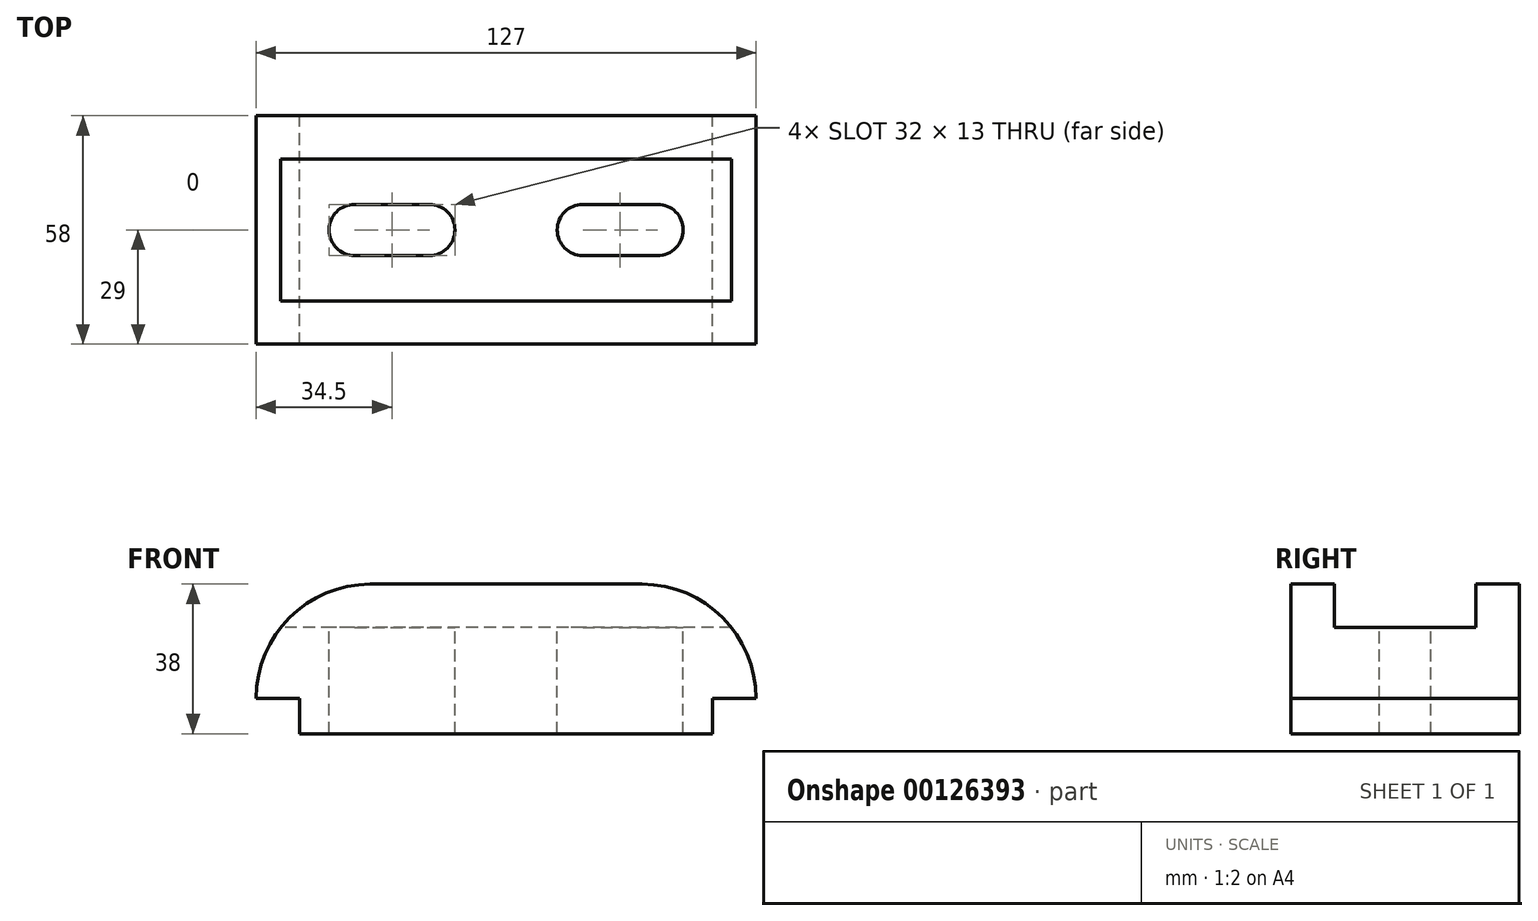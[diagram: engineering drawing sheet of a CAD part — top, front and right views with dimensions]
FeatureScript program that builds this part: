
annotation { "Feature Type Name" : "Feature", "Feature Type Description" : "" }
export const myFeature = defineFeature(function(context is Context, id is Id, definition is map)
    precondition{}
    {
        {
            var Q0;
            Q0=qCreatedBy(makeId("Front.planeOp"),FACE);
            var sketch = newSketch(context, id + "F0", { "sketchPlane" : qUnion([Q0])});
            skLineSegment(sketch, "E0.bottom", {"start": v(0, 0) * mm, "end": v(127, 0) * mm});
            skLineSegment(sketch, "E0.top", {"start": v(29, 38) * mm, "end": v(98, 38) * mm});
            skLineSegment(sketch, "E0.left", {"start": v(0, 0) * mm, "end": v(0, 9) * mm});
            skLineSegment(sketch, "E0.right", {"start": v(127, 0) * mm, "end": v(127, 9) * mm});
            skLineSegment(sketch, "E1", {"start": v(0, 9) * mm, "end": v(11, 9) * mm});
            skLineSegment(sketch, "E2", {"start": v(11, 9) * mm, "end": v(11, 0) * mm});
            skLineSegment(sketch, "E3.bottom", {"start": v(127, 0) * mm, "end": v(116, 0) * mm});
            skLineSegment(sketch, "E3.top", {"start": v(127, 9) * mm, "end": v(116, 9) * mm});
            skLineSegment(sketch, "E3.right", {"start": v(116, 0) * mm, "end": v(116, 9) * mm});
            skArc(sketch, "E4", {"start": v(0, 9) * mm, "mid": v(8.5, 29.5) * mm, "end": v(29, 38) * mm});
            skPoint(sketch, "E4.centerSnap0", {"position": v(5.5, 9) * mm});
            skArc(sketch, "E5", {"start": v(127, 9) * mm, "mid": v(118.5, 29.5) * mm, "end": v(98, 38) * mm});
            skSolve(sketch);
        }
        {
            var Q0;
            Q0=makeQuery(id+"F0.imprint","IMPRINT",FACE,{"disambiguationData":[TD([[makeQuery(id+"F0.imprint","IMPRINT",EDGE,{"derivedFrom":sQuery(id+"F0.wireOp",EDGE,"E0.top")}),-1.0]])]});
            extrude(context, id + "F1", {"entities" : qUnion([Q0]), "endBound" : BoundingType.SYMMETRIC, "depth" : 58 * mm});
        }
        {
            var Q0;
            Q0=makeQuery(id+"F1.opExtrude","SWEPT_FACE",FACE,{"disambiguationData":[OSD([sQuery(id+"F0.wireOp",EDGE,"E0.top")])]});
            var sketch = newSketch(context, id + "F2", { "sketchPlane" : qUnion([Q0])});
            skArc(sketch, "E6", {"start": v(25, 6.5) * mm, "mid": v(18.5, 0) * mm, "end": v(25, -6.5) * mm});
            skPoint(sketch, "E6.centerSnap0", {"position": v(29, 0) * mm});
            skArc(sketch, "E7", {"start": v(44, -6.5) * mm, "mid": v(50.5, 0) * mm, "end": v(44, 6.5) * mm});
            skArc(sketch, "E8", {"start": v(83, 6.5) * mm, "mid": v(76.5, 0) * mm, "end": v(83, -6.5) * mm});
            skArc(sketch, "E9", {"start": v(102, -6.5) * mm, "mid": v(108.5, 0) * mm, "end": v(102, 6.5) * mm});
            skLineSegment(sketch, "E10", {"start": v(25, 6.5) * mm, "end": v(44, 6.5) * mm});
            skLineSegment(sketch, "E11", {"start": v(25, -6.5) * mm, "end": v(44, -6.5) * mm});
            skLineSegment(sketch, "E12", {"start": v(83, 6.5) * mm, "end": v(102, 6.5) * mm});
            skLineSegment(sketch, "E13", {"start": v(83, -6.5) * mm, "end": v(102, -6.5) * mm});
            skSolve(sketch);
        }
        {
            var Q0;
            Q0 = qSketchRegion(id + "F2", true);
            extrude(context, id + "F3", {"entities" : qUnion([Q0]), "operationType" : NewBodyOperationType.REMOVE, "endBound" : BoundingType.THROUGH_ALL, "oppositeDirection" : true, "depth" : 25 * mm});
        }
        {
            var Q0;
            Q0=qCreatedBy(makeId("Right.planeOp"),FACE);
            var sketch = newSketch(context, id + "F4", { "sketchPlane" : qUnion([Q0])});
            skLineSegment(sketch, "E14.bottom", {"start": v(18, 38) * mm, "end": v(-18, 38) * mm});
            skLineSegment(sketch, "E14.top", {"start": v(18, 27) * mm, "end": v(-18, 27) * mm});
            skLineSegment(sketch, "E14.left", {"start": v(18, 38) * mm, "end": v(18, 27) * mm});
            skLineSegment(sketch, "E14.right", {"start": v(-18, 38) * mm, "end": v(-18, 27) * mm});
            skSolve(sketch);
        }
        {
            var Q0;
            Q0 = qSketchRegion(id + "F4", true);
            extrude(context, id + "F5", {"entities" : qUnion([Q0]), "operationType" : NewBodyOperationType.REMOVE, "endBound" : BoundingType.THROUGH_ALL, "depth" : 25 * mm});
        }
    });
